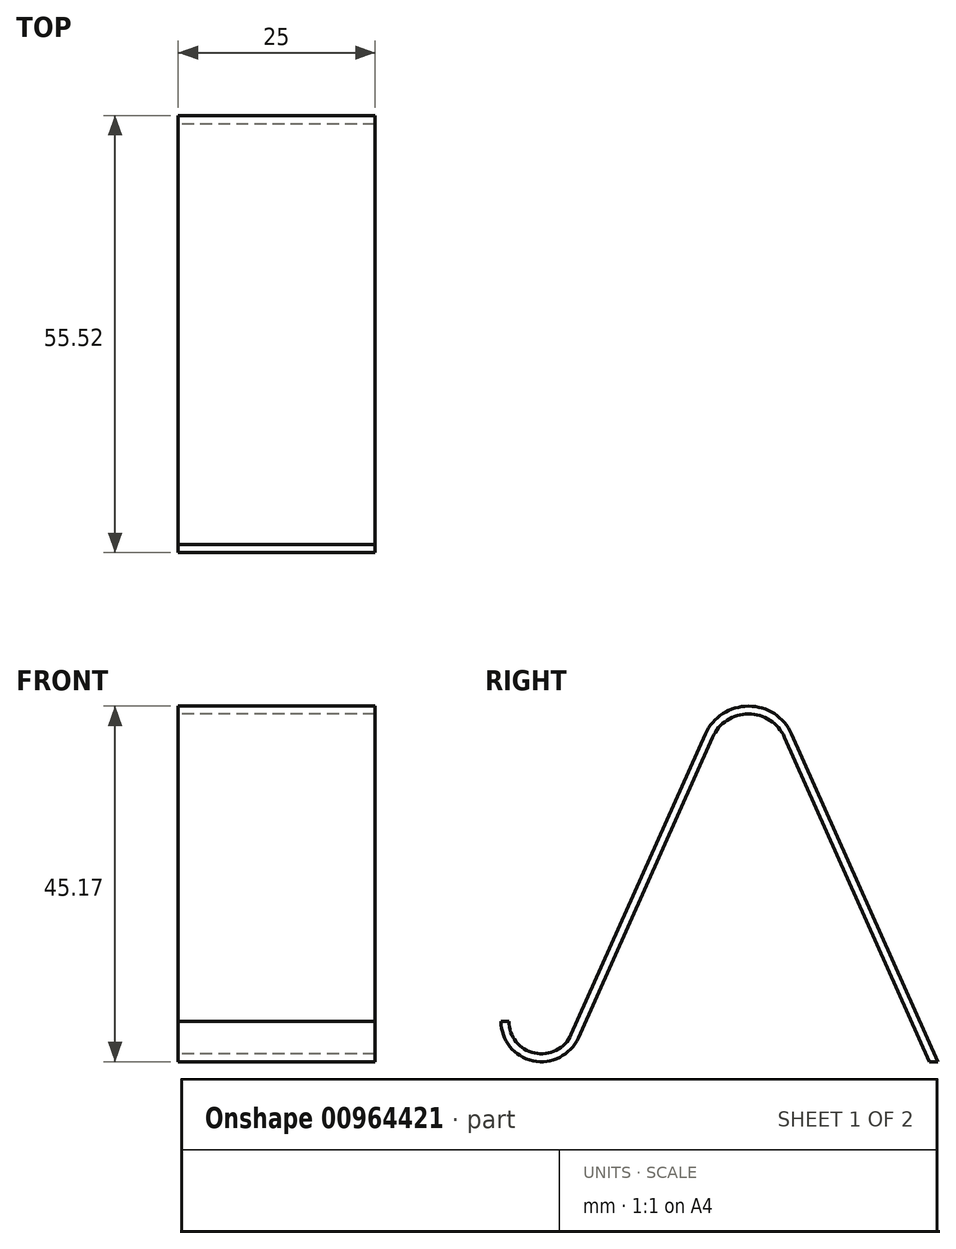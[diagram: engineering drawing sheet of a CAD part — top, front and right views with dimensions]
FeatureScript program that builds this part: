
annotation { "Feature Type Name" : "Feature", "Feature Type Description" : "" }
export const myFeature = defineFeature(function(context is Context, id is Id, definition is map)
    precondition{}
    {
        {
            var Q0;
            Q0=qCreatedBy(makeId("Right.planeOp"),FACE);
            var sketch = newSketch(context, id + "F0", { "sketchPlane" : qUnion([Q0])});
            skLineSegment(sketch, "E0", {"start": v(-21.62, 3.04) * mm, "end": v(-4.57, 41.2) * mm});
            skLineSegment(sketch, "E1", {"start": v(0, 38.41) * mm, "end": v(0, -33) * mm, "construction": true});
            skLineSegment(sketch, "E2.MirrorCS", {"start": v(22.98, 0) * mm, "end": v(4.57, 41.2) * mm});
            skArc(sketch, "E3", {"start": v(-31.45, 5.14) * mm, "mid": v(-27.38, 0.11) * mm, "end": v(-21.62, 3.04) * mm});
            skPoint(sketch, "E4.orphan", {"position": v(-22.98, 0) * mm});
            skPoint(sketch, "E5.visualSharp", {"position": v(0, 51.42) * mm});
            skArc(sketch, "E5.filletArc", {"start": v(4.57, 41.2) * mm, "mid": v(0, 44.17) * mm, "end": v(-4.57, 41.2) * mm});
            skLineSegment(sketch, "E6.0", {"start": v(24.07, 0) * mm, "end": v(5.48, 41.62) * mm});
            skLineSegment(sketch, "E7.0", {"start": v(-22.53, 3.45) * mm, "end": v(-5.48, 41.62) * mm});
            skArc(sketch, "E7.1", {"start": v(5.48, 41.62) * mm, "mid": v(0, 45.17) * mm, "end": v(-5.48, 41.62) * mm});
            skArc(sketch, "E8.0", {"start": v(-30.45, 5.14) * mm, "mid": v(-27.17, 1.1) * mm, "end": v(-22.53, 3.45) * mm});
            skLineSegment(sketch, "E9", {"start": v(-31.45, 5.14) * mm, "end": v(-30.45, 5.14) * mm});
            skLineSegment(sketch, "E10", {"start": v(22.98, 0) * mm, "end": v(24.07, 0) * mm});
            skSolve(sketch);
        }
        {
            var Q0;
            Q0 = qSketchRegion(id + "F0", true);
            extrude(context, id + "F1", {"entities" : qUnion([Q0]), "depth" : 25 * mm, "offsetDistance" : 25 * mm});
        }
    });
